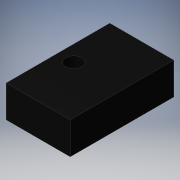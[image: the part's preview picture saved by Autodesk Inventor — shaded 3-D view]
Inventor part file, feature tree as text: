
AUTODESK INVENTOR PART (.ipt)
format: ipt  version: 2016 (Build 200138000, 138)  size: 95,232 bytes
history: native  units: in
note: dims shown in document units (in); Inventor stores cm internally (conversion verified against a paired STEP export)
features: extrude x1, sketch x1
ambient origin geometry x8: Origin, YZ Plane, XZ Plane, XY Plane, X Axis, Y Axis, Z Axis, Center Point
bodies: Solid1 (feature_tree)
feature tree (2):
  extrude  "Extrusion1"  Depth=3.2361in
  sketch  "Sketch1"  dims[d0=2.0in d1=3.2361in d2=0.5in d3=0.5in d4=1.0in d5=0.0in]
